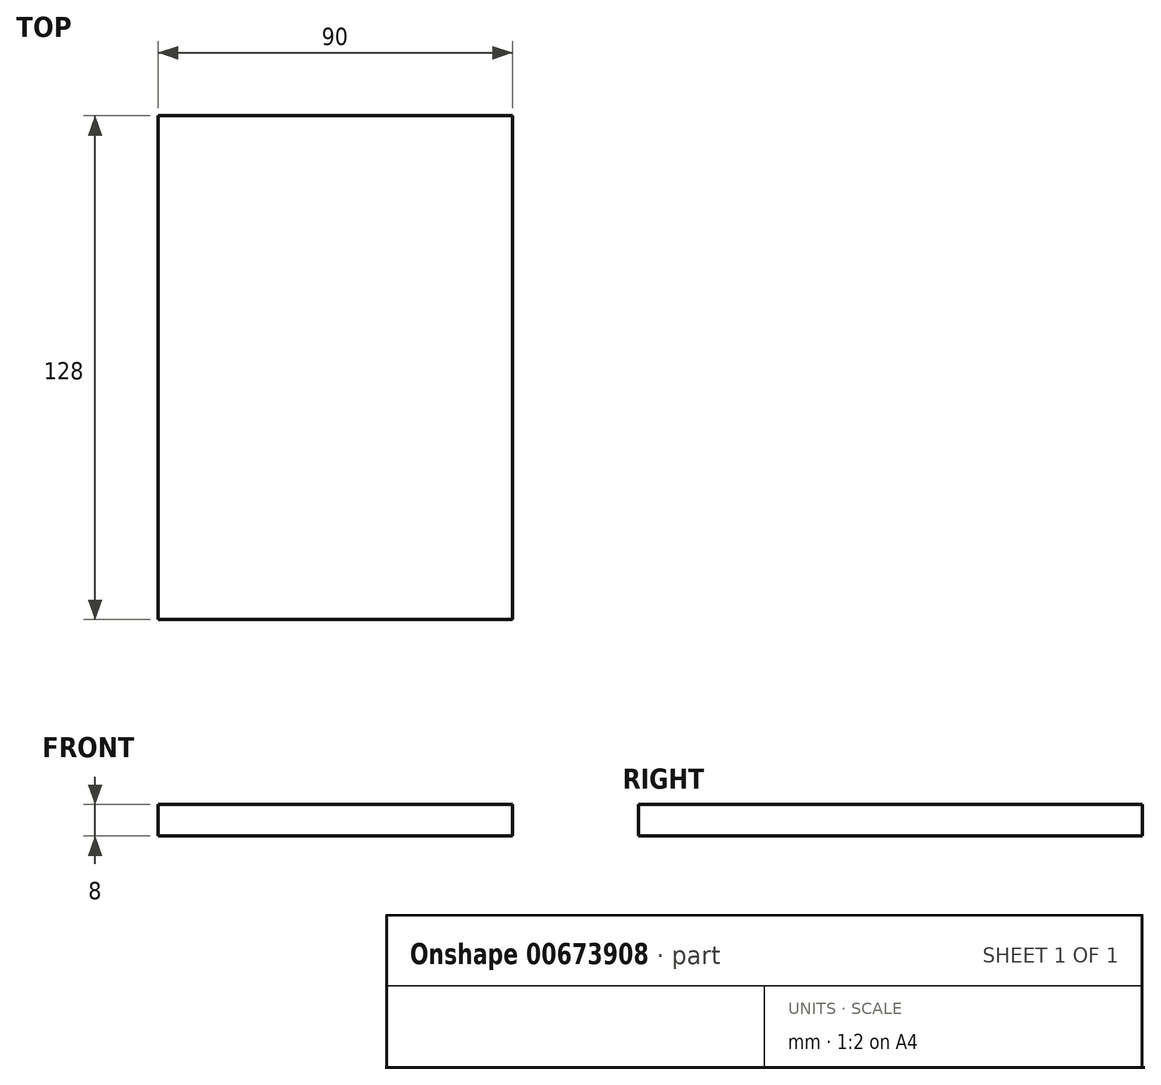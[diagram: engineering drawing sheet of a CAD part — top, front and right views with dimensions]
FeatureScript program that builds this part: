
annotation { "Feature Type Name" : "Feature", "Feature Type Description" : "" }
export const myFeature = defineFeature(function(context is Context, id is Id, definition is map)
    precondition{}
    {
        {
            var Q0;
            Q0=qCreatedBy(makeId("Top.planeOp"),FACE);
            var sketch = newSketch(context, id + "F0", { "sketchPlane" : qUnion([Q0])});
            skLineSegment(sketch, "E0.bottom", {"start": v(-29.48, 104.4) * mm, "end": v(60.52, 104.4) * mm});
            skLineSegment(sketch, "E0.top", {"start": v(-29.48, -23.6) * mm, "end": v(60.52, -23.6) * mm});
            skLineSegment(sketch, "E0.left", {"start": v(-29.48, 104.4) * mm, "end": v(-29.48, -23.6) * mm});
            skLineSegment(sketch, "E0.right", {"start": v(60.52, 104.4) * mm, "end": v(60.52, -23.6) * mm});
            skSolve(sketch);
        }
        {
            var Q0;
            Q0=makeQuery(id+"F0.imprint","IMPRINT",FACE,{"disambiguationData":[TD([[makeQuery(id+"F0.imprint","IMPRINT",EDGE,{"derivedFrom":sQuery(id+"F0.wireOp",EDGE,"E0.bottom")}),-1.0]])]});
            extrude(context, id + "F1", {"entities" : qUnion([Q0]), "depth" : 8 * mm, "offsetDistance" : 25 * mm});
        }
    });
